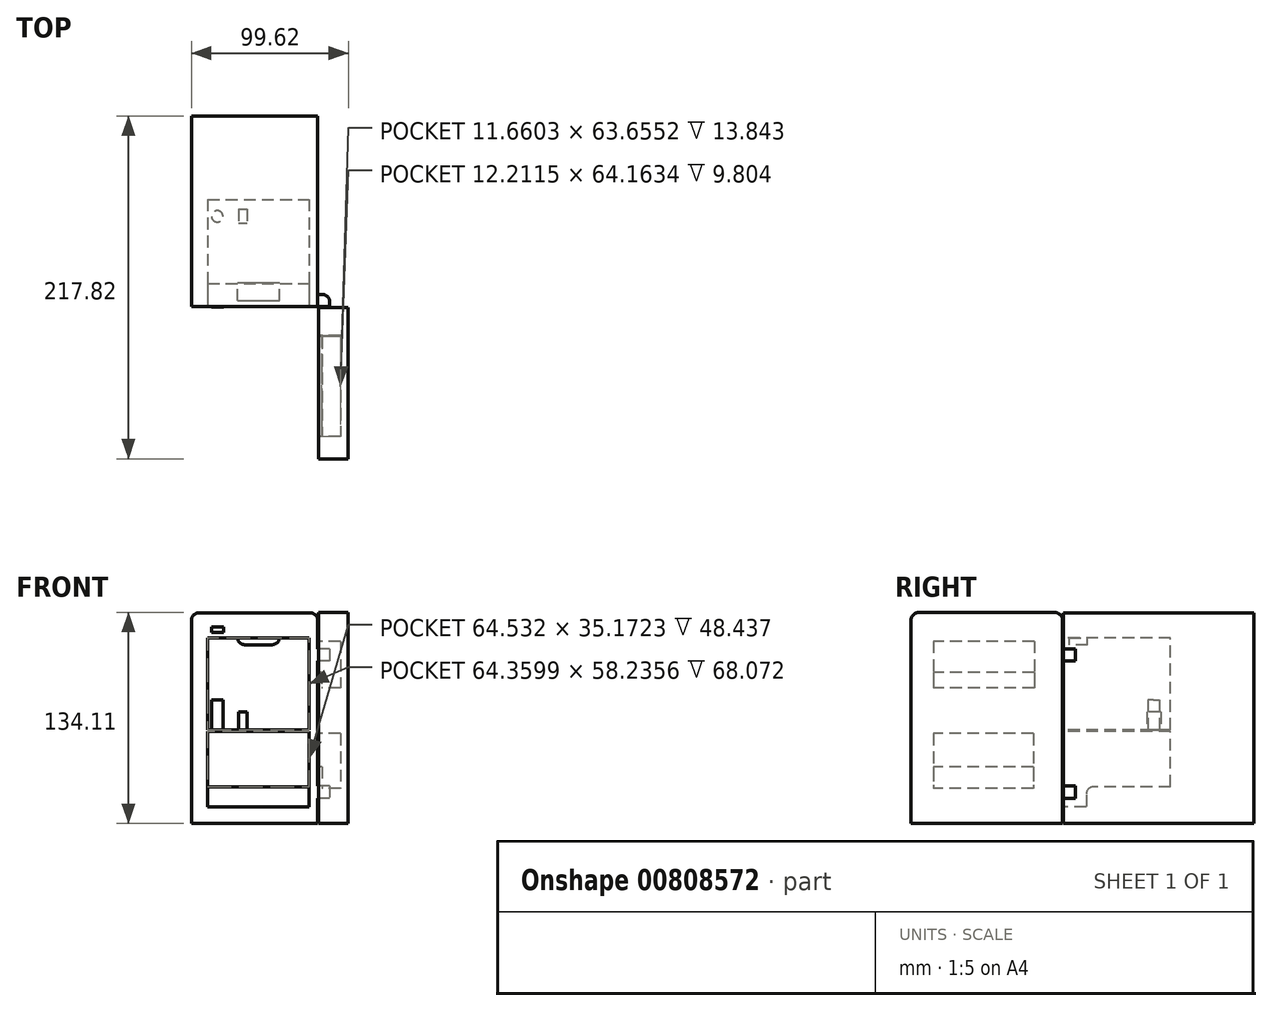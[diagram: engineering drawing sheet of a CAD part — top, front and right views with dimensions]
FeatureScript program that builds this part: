
annotation { "Feature Type Name" : "Feature", "Feature Type Description" : "" }
export const myFeature = defineFeature(function(context is Context, id is Id, definition is map)
    precondition{}
    {
        {
            var Q0;
            Q0=qCreatedBy(makeId("Top.planeOp"),FACE);
            var sketch = newSketch(context, id + "F0", { "sketchPlane" : qUnion([Q0])});
            skLineSegment(sketch, "E0.bottom", {"start": v(-38.44, 50.05) * mm, "end": v(41.76, 50.05) * mm});
            skLineSegment(sketch, "E0.top", {"start": v(-38.44, -71.07) * mm, "end": v(41.76, -71.07) * mm});
            skLineSegment(sketch, "E0.left", {"start": v(-38.44, 50.05) * mm, "end": v(-38.44, -71.07) * mm});
            skLineSegment(sketch, "E0.right", {"start": v(41.76, 50.05) * mm, "end": v(41.76, -71.07) * mm});
            skSolve(sketch);
        }
        {
            var Q0;
            Q0 = qSketchRegion(id + "F0", true);
            extrude(context, id + "F1", {"entities" : qUnion([Q0]), "depth" : 133.86 * mm, "offsetDistance" : 25.4 * mm});
        }
        {
            var Q0;
            Q0=qCreatedBy(makeId("Top.planeOp"),FACE);
            var sketch = newSketch(context, id + "F2", { "sketchPlane" : qUnion([Q0])});
            skLineSegment(sketch, "E1.bottom", {"start": v(42.32, -71.47) * mm, "end": v(61.18, -71.47) * mm});
            skLineSegment(sketch, "E1.top", {"start": v(42.32, -167.77) * mm, "end": v(61.18, -167.77) * mm});
            skLineSegment(sketch, "E1.left", {"start": v(42.32, -71.47) * mm, "end": v(42.32, -167.77) * mm});
            skLineSegment(sketch, "E1.right", {"start": v(61.18, -71.47) * mm, "end": v(61.18, -167.77) * mm});
            skSolve(sketch);
        }
        {
            var Q0;
            Q0=makeQuery(id+"F2.imprint","IMPRINT",FACE,{"disambiguationData":[TD([[makeQuery(id+"F2.imprint","IMPRINT",EDGE,{"derivedFrom":sQuery(id+"F2.wireOp",EDGE,"E1.bottom")}),-1.0]])]});
            extrude(context, id + "F3", {"entities" : qUnion([Q0]), "depth" : 134.11 * mm, "offsetDistance" : 25.4 * mm});
        }
        {
            var Q0;
            Q0=makeQuery(id+"F3.opExtrude","SWEPT_FACE",FACE,{"disambiguationData":[OSD([sQuery(id+"F2.wireOp",EDGE,"E1.left")])]});
            var sketch = newSketch(context, id + "F4", { "sketchPlane" : qUnion([Q0])});
            skLineSegment(sketch, "E2.bottom", {"start": v(89.5, 115.7) * mm, "end": v(153.66, 115.7) * mm});
            skLineSegment(sketch, "E2.top", {"start": v(89.5, 86.24) * mm, "end": v(153.66, 86.24) * mm});
            skLineSegment(sketch, "E2.left", {"start": v(89.5, 115.7) * mm, "end": v(89.5, 86.24) * mm});
            skLineSegment(sketch, "E2.right", {"start": v(153.66, 115.7) * mm, "end": v(153.66, 86.24) * mm});
            skLineSegment(sketch, "E3.bottom", {"start": v(90, 57.2) * mm, "end": v(153.66, 57.2) * mm});
            skLineSegment(sketch, "E3.top", {"start": v(90, 22.28) * mm, "end": v(153.66, 22.28) * mm});
            skLineSegment(sketch, "E3.left", {"start": v(90, 57.2) * mm, "end": v(90, 22.28) * mm});
            skLineSegment(sketch, "E3.right", {"start": v(153.66, 57.2) * mm, "end": v(153.66, 22.28) * mm});
            skSolve(sketch);
        }
        {
            var Q0;
            Q0=makeQuery(id+"F4.imprint","IMPRINT",FACE,{"disambiguationData":[TD([[makeQuery(id+"F4.imprint","IMPRINT",EDGE,{"derivedFrom":sQuery(id+"F4.wireOp",EDGE,"E2.bottom")}),-1.0]])]});
            var Q1;
            Q1=makeQuery(id+"F4.imprint","IMPRINT",FACE,{"disambiguationData":[TD([[makeQuery(id+"F4.imprint","IMPRINT",EDGE,{"derivedFrom":sQuery(id+"F4.wireOp",EDGE,"E3.bottom")}),-1.0]])]});
            extrude(context, id + "F5", {"entities" : qUnion([Q0, Q1]), "operationType" : NewBodyOperationType.REMOVE, "oppositeDirection" : true, "depth" : 13.97 * mm, "offsetDistance" : 25.4 * mm});
        }
        {
            var Q0;
            Q0=makeQuery(id+"F5.boolean.opBoolean","COPY",FACE,{"derivedFrom":makeQuery(id+"F5.opExtrude","SWEPT_FACE",FACE,{"disambiguationData":[OSD([sQuery(id+"F4.wireOp",EDGE,"E2.top")])]})});
            var sketch = newSketch(context, id + "F6", { "sketchPlane" : qUnion([Q0])});
            skLineSegment(sketch, "E4.bottom", {"start": v(44.08, -89.5) * mm, "end": v(42.32, -89.5) * mm});
            skLineSegment(sketch, "E4.top", {"start": v(44.08, -153.66) * mm, "end": v(42.32, -153.66) * mm});
            skLineSegment(sketch, "E4.left", {"start": v(44.08, -89.5) * mm, "end": v(44.08, -153.66) * mm});
            skLineSegment(sketch, "E4.right", {"start": v(42.32, -89.5) * mm, "end": v(42.32, -153.66) * mm});
            skSolve(sketch);
        }
        {
            var Q0;
            Q0=makeQuery(id+"F6.imprint","IMPRINT",FACE,{"disambiguationData":[TD([[makeQuery(id+"F6.imprint","IMPRINT",EDGE,{"derivedFrom":sQuery(id+"F6.wireOp",EDGE,"E4.bottom")}),1.0]])]});
            extrude(context, id + "F7", {"entities" : qUnion([Q0]), "operationType" : NewBodyOperationType.ADD, "depth" : 9.8 * mm, "offsetDistance" : 25.4 * mm});
        }
        {
            var Q0;
            Q0=makeQuery(id+"F5.boolean.opBoolean","COPY",FACE,{"derivedFrom":makeQuery(id+"F5.opExtrude","SWEPT_FACE",FACE,{"disambiguationData":[OSD([sQuery(id+"F4.wireOp",EDGE,"E3.top")])]})});
            var sketch = newSketch(context, id + "F8", { "sketchPlane" : qUnion([Q0])});
            skLineSegment(sketch, "E5.bottom", {"start": v(44.63, -90) * mm, "end": v(42.32, -90) * mm});
            skLineSegment(sketch, "E5.top", {"start": v(44.63, -153.66) * mm, "end": v(42.32, -153.66) * mm});
            skLineSegment(sketch, "E5.left", {"start": v(44.63, -90) * mm, "end": v(44.63, -153.66) * mm});
            skLineSegment(sketch, "E5.right", {"start": v(42.32, -90) * mm, "end": v(42.32, -153.66) * mm});
            skSolve(sketch);
        }
        {
            var Q0;
            Q0=makeQuery(id+"F8.imprint","IMPRINT",FACE,{"disambiguationData":[TD([[makeQuery(id+"F8.imprint","IMPRINT",EDGE,{"derivedFrom":sQuery(id+"F8.wireOp",EDGE,"E5.bottom")}),1.0]])]});
            extrude(context, id + "F9", {"entities" : qUnion([Q0]), "operationType" : NewBodyOperationType.ADD, "depth" : 13.84 * mm, "offsetDistance" : 25.4 * mm});
        }
        {
            var Q0;
            Q0=makeQuery(id+"F1.opExtrude","CAP_EDGE",EDGE,{"disambiguationData":[OSD([sQuery(id+"F0.wireOp",EDGE,"E0.left")])],"isStart":false});
            var Q1;
            Q1=makeQuery(id+"F1.opExtrude","CAP_EDGE",EDGE,{"disambiguationData":[OSD([sQuery(id+"F0.wireOp",EDGE,"E0.right")])],"isStart":false});
            var Q2;
            Q2=makeQuery(id+"F3.opExtrude","CAP_EDGE",EDGE,{"disambiguationData":[OSD([sQuery(id+"F2.wireOp",EDGE,"E1.top")])],"isStart":false});
            var Q3;
            Q3=makeQuery(id+"F3.opExtrude","CAP_EDGE",EDGE,{"disambiguationData":[OSD([sQuery(id+"F2.wireOp",EDGE,"E1.bottom")])],"isStart":false});
            fillet(context, id + "F10", {"entities" : qUnion([Q0, Q1, Q2, Q3]), "radius" : 5.08 * mm, "tangentPropagation" : true, "allowEdgeOverflow" : false});
        }
        {
            var Q0;
            Q0=makeQuery(id+"F1.opExtrude","SWEPT_FACE",FACE,{"disambiguationData":[OSD([sQuery(id+"F0.wireOp",EDGE,"E0.right")])]});
            var sketch = newSketch(context, id + "F11", { "sketchPlane" : qUnion([Q0])});
            skLineSegment(sketch, "E6.bottom", {"start": v(-71.07, 110.8) * mm, "end": v(-63.22, 110.8) * mm});
            skLineSegment(sketch, "E6.top", {"start": v(-71.07, 103.4) * mm, "end": v(-63.22, 103.4) * mm});
            skLineSegment(sketch, "E6.left", {"start": v(-71.07, 110.8) * mm, "end": v(-71.07, 103.4) * mm});
            skLineSegment(sketch, "E6.right", {"start": v(-63.22, 110.8) * mm, "end": v(-63.22, 103.4) * mm});
            skLineSegment(sketch, "E7.bottom", {"start": v(-71.07, 24.04) * mm, "end": v(-63.22, 24.04) * mm});
            skLineSegment(sketch, "E7.top", {"start": v(-71.07, 15.97) * mm, "end": v(-63.22, 15.97) * mm});
            skLineSegment(sketch, "E7.left", {"start": v(-71.07, 24.04) * mm, "end": v(-71.07, 15.97) * mm});
            skLineSegment(sketch, "E7.right", {"start": v(-63.22, 24.04) * mm, "end": v(-63.22, 15.97) * mm});
            skSolve(sketch);
        }
        {
            var Q0;
            Q0=makeQuery(id+"F11.imprint","IMPRINT",FACE,{"disambiguationData":[TD([[makeQuery(id+"F11.imprint","IMPRINT",EDGE,{"derivedFrom":sQuery(id+"F11.wireOp",EDGE,"E6.bottom")}),-1.0]])]});
            var Q1;
            Q1=makeQuery(id+"F11.imprint","IMPRINT",FACE,{"disambiguationData":[TD([[makeQuery(id+"F11.imprint","IMPRINT",EDGE,{"derivedFrom":sQuery(id+"F11.wireOp",EDGE,"E7.bottom")}),-1.0]])]});
            extrude(context, id + "F12", {"entities" : qUnion([Q0, Q1]), "operationType" : NewBodyOperationType.ADD, "depth" : 7.62 * mm, "offsetDistance" : 25.4 * mm});
        }
        {
            var Q0;
            Q0=makeQuery(id+"F12.opExtrude","CAP_EDGE",EDGE,{"disambiguationData":[OSD([sQuery(id+"F11.wireOp",EDGE,"E6.right")])],"isStart":false});
            var Q1;
            Q1=makeQuery(id+"F12.opExtrude","CAP_EDGE",EDGE,{"disambiguationData":[OSD([sQuery(id+"F11.wireOp",EDGE,"E7.right")])],"isStart":false});
            fillet(context, id + "F13", {"entities" : qUnion([Q0, Q1]), "radius" : 5.08 * mm, "tangentPropagation" : true, "allowEdgeOverflow" : false});
        }
        {
            var Q0;
            Q0=makeQuery(id+"F12.boolean.opBoolean","MERGE",FACE,{"derivedFrom":[makeQuery(id+"F1.opExtrude","SWEPT_FACE",FACE,{"disambiguationData":[OSD([sQuery(id+"F0.wireOp",EDGE,"E0.top")])]}),makeQuery(id+"F12.opExtrude","SWEPT_FACE",FACE,{"disambiguationData":[OSD([sQuery(id+"F11.wireOp",EDGE,"E6.left")])]}),makeQuery(id+"F12.opExtrude","SWEPT_FACE",FACE,{"disambiguationData":[OSD([sQuery(id+"F11.wireOp",EDGE,"E7.left")])]})]});
            var sketch = newSketch(context, id + "F14", { "sketchPlane" : qUnion([Q0])});
            skLineSegment(sketch, "E8.bottom", {"start": v(-28.17, 10.71) * mm, "end": v(36.36, 10.71) * mm});
            skLineSegment(sketch, "E8.top", {"start": v(-28.17, 58.58) * mm, "end": v(36.36, 58.58) * mm});
            skLineSegment(sketch, "E8.left", {"start": v(-28.17, 10.71) * mm, "end": v(-28.17, 58.58) * mm});
            skLineSegment(sketch, "E8.right", {"start": v(36.36, 10.71) * mm, "end": v(36.36, 58.58) * mm});
            skLineSegment(sketch, "E9.bottom", {"start": v(-28.17, 66.66) * mm, "end": v(36.2, 66.66) * mm});
            skLineSegment(sketch, "E9.top", {"start": v(-28.17, 117.78) * mm, "end": v(36.2, 117.78) * mm});
            skLineSegment(sketch, "E9.left", {"start": v(-28.17, 66.66) * mm, "end": v(-28.17, 117.78) * mm});
            skLineSegment(sketch, "E9.right", {"start": v(36.2, 66.66) * mm, "end": v(36.2, 117.78) * mm});
            skSolve(sketch);
        }
        {
            var Q0;
            Q0=makeQuery(id+"F14.imprint","IMPRINT",FACE,{"disambiguationData":[TD([[makeQuery(id+"F14.imprint","IMPRINT",EDGE,{"derivedFrom":sQuery(id+"F14.wireOp",EDGE,"E9.bottom")}),1.0]])]});
            var Q1;
            Q1=makeQuery(id+"F14.imprint","IMPRINT",FACE,{"disambiguationData":[TD([[makeQuery(id+"F14.imprint","IMPRINT",EDGE,{"derivedFrom":sQuery(id+"F14.wireOp",EDGE,"E8.bottom")}),1.0]])]});
            extrude(context, id + "F15", {"entities" : qUnion([Q0, Q1]), "operationType" : NewBodyOperationType.REMOVE, "oppositeDirection" : true, "depth" : 68.07 * mm, "offsetDistance" : 25.4 * mm});
        }
        {
            var Q0;
            Q0=makeQuery(id+"F15.boolean.opBoolean","COPY",FACE,{"derivedFrom":makeQuery(id+"F15.opExtrude","SWEPT_FACE",FACE,{"disambiguationData":[OSD([sQuery(id+"F14.wireOp",EDGE,"E9.bottom")])]})});
            extrude(context, id + "F16", {"entities" : qUnion([Q0]), "operationType" : NewBodyOperationType.REMOVE, "oppositeDirection" : true, "depth" : 7.11 * mm, "offsetDistance" : 25.4 * mm});
        }
        {
            var Q0;
            Q0=makeQuery(id+"F15.boolean.opBoolean","COPY",FACE,{"derivedFrom":makeQuery(id+"F15.opExtrude","SWEPT_FACE",FACE,{"disambiguationData":[OSD([sQuery(id+"F14.wireOp",EDGE,"E8.bottom")])]})});
            var sketch = newSketch(context, id + "F17", { "sketchPlane" : qUnion([Q0])});
            skLineSegment(sketch, "E10.bottom", {"start": v(-28.17, -56.51) * mm, "end": v(0, -56.51) * mm});
            skLineSegment(sketch, "E10.top", {"start": v(-28.17, -3) * mm, "end": v(0, -3) * mm});
            skLineSegment(sketch, "E10.left", {"start": v(-28.17, -56.51) * mm, "end": v(-28.17, -3) * mm});
            skLineSegment(sketch, "E10.right", {"start": v(0, -56.51) * mm, "end": v(0, -3) * mm});
            skLineSegment(sketch, "E11.bottom", {"start": v(0, -56.51) * mm, "end": v(36.36, -56.51) * mm});
            skLineSegment(sketch, "E11.top", {"start": v(0, -3) * mm, "end": v(36.36, -3) * mm});
            skLineSegment(sketch, "E11.right", {"start": v(36.36, -56.51) * mm, "end": v(36.36, -3) * mm});
            skSolve(sketch);
        }
        {
            var Q0;
            Q0=makeQuery(id+"F17.imprint","IMPRINT",FACE,{"disambiguationData":[TD([[makeQuery(id+"F17.imprint","IMPRINT",EDGE,{"derivedFrom":sQuery(id+"F17.wireOp",EDGE,"E10.bottom")}),1.0]])]});
            var Q1;
            Q1=makeQuery(id+"F17.imprint","IMPRINT",FACE,{"disambiguationData":[TD([[makeQuery(id+"F17.imprint","IMPRINT",EDGE,{"derivedFrom":sQuery(id+"F17.wireOp",EDGE,"E11.bottom")}),1.0]])]});
            extrude(context, id + "F18", {"entities" : qUnion([Q0, Q1]), "operationType" : NewBodyOperationType.ADD, "depth" : 12.7 * mm, "offsetDistance" : 25.4 * mm});
        }
        {
            var Q0;
            Q0=makeQuery(id+"F18.opExtrude","CAP_EDGE",EDGE,{"disambiguationData":[OSD([sQuery(id+"F17.wireOp",EDGE,"E10.bottom"),sQuery(id+"F17.wireOp",EDGE,"E11.bottom")])],"isStart":false});
            fillet(context, id + "F19", {"entities" : qUnion([Q0]), "radius" : 5.08 * mm, "tangentPropagation" : true, "allowEdgeOverflow" : false});
        }
        {
            var Q0;
            Q0=makeQuery(id+"F12.boolean.opBoolean","MERGE",FACE,{"derivedFrom":[makeQuery(id+"F1.opExtrude","SWEPT_FACE",FACE,{"disambiguationData":[OSD([sQuery(id+"F0.wireOp",EDGE,"E0.top")])]}),makeQuery(id+"F12.opExtrude","SWEPT_FACE",FACE,{"disambiguationData":[OSD([sQuery(id+"F11.wireOp",EDGE,"E6.left")])]}),makeQuery(id+"F12.opExtrude","SWEPT_FACE",FACE,{"disambiguationData":[OSD([sQuery(id+"F11.wireOp",EDGE,"E7.left")])]})]});
            var sketch = newSketch(context, id + "F20", { "sketchPlane" : qUnion([Q0])});
            skLineSegment(sketch, "E12.bottom", {"start": v(-25.78, 121.5) * mm, "end": v(-18, 121.5) * mm});
            skLineSegment(sketch, "E12.top", {"start": v(-25.78, 125) * mm, "end": v(-18, 125) * mm});
            skLineSegment(sketch, "E12.left", {"start": v(-25.78, 121.5) * mm, "end": v(-25.78, 125) * mm});
            skLineSegment(sketch, "E12.right", {"start": v(-18, 121.5) * mm, "end": v(-18, 125) * mm});
            skSolve(sketch);
        }
        {
            var Q0;
            Q0=makeQuery(id+"F20.imprint","IMPRINT",FACE,{"disambiguationData":[TD([[makeQuery(id+"F20.imprint","IMPRINT",EDGE,{"derivedFrom":sQuery(id+"F20.wireOp",EDGE,"E12.bottom")}),1.0]])]});
            extrude(context, id + "F21", {"entities" : qUnion([Q0]), "operationType" : NewBodyOperationType.ADD, "depth" : 0.23 * mm, "offsetDistance" : 25.4 * mm});
        }
        {
            var Q0;
            Q0=makeQuery(id+"F15.boolean.opBoolean","COPY",FACE,{"derivedFrom":makeQuery(id+"F15.opExtrude","SWEPT_FACE",FACE,{"disambiguationData":[OSD([sQuery(id+"F14.wireOp",EDGE,"E9.top")])]})});
            var sketch = newSketch(context, id + "F22", { "sketchPlane" : qUnion([Q0])});
            skLineSegment(sketch, "E13.bottom", {"start": v(-9.29, 67.33) * mm, "end": v(17.64, 67.33) * mm});
            skLineSegment(sketch, "E13.top", {"start": v(-9.29, 55.68) * mm, "end": v(17.64, 55.68) * mm});
            skLineSegment(sketch, "E13.left", {"start": v(-9.29, 67.33) * mm, "end": v(-9.29, 55.68) * mm});
            skLineSegment(sketch, "E13.right", {"start": v(17.64, 67.33) * mm, "end": v(17.64, 55.68) * mm});
            skSolve(sketch);
        }
        {
            var Q0;
            Q0=makeQuery(id+"F22.imprint","IMPRINT",FACE,{"disambiguationData":[TD([[makeQuery(id+"F22.imprint","IMPRINT",EDGE,{"derivedFrom":sQuery(id+"F22.wireOp",EDGE,"E13.bottom")}),-1.0]])]});
            extrude(context, id + "F23", {"entities" : qUnion([Q0]), "operationType" : NewBodyOperationType.ADD, "depth" : 4.24 * mm, "offsetDistance" : 25.4 * mm});
        }
        {
            var Q0;
            Q0=makeQuery(id+"F23.opExtrude","CAP_EDGE",EDGE,{"disambiguationData":[OSD([sQuery(id+"F22.wireOp",EDGE,"E13.left")])],"isStart":false});
            var Q1;
            Q1=makeQuery(id+"F23.opExtrude","CAP_EDGE",EDGE,{"disambiguationData":[OSD([sQuery(id+"F22.wireOp",EDGE,"E13.right")])],"isStart":false});
            fillet(context, id + "F24", {"entities" : qUnion([Q0, Q1]), "radius" : 5.08 * mm, "tangentPropagation" : true, "allowEdgeOverflow" : false});
        }
        {
            var Q0;
            Q0=makeQuery(id+"F16.boolean.opBoolean","COPY",FACE,{"derivedFrom":makeQuery(id+"F16.opExtrude","CAP_FACE",FACE,{"disambiguationData":[OSD([sQuery(id+"F14.wireOp",EDGE,"E9.bottom")])],"isStart":false})});
            var sketch = newSketch(context, id + "F25", { "sketchPlane" : qUnion([Q0])});
            skCircle(sketch, "E14", {"center": v(-22.06, -13.7) * mm, "radius": 3.62 * mm});
            skSolve(sketch);
        }
        {
            var Q0;
            Q0=makeQuery(id+"F25.imprint","IMPRINT",FACE,{"disambiguationData":[TD([[makeQuery(id+"F25.imprint","IMPRINT",EDGE,{"derivedFrom":sQuery(id+"F25.wireOp",EDGE,"E14")}),1.0]])]});
            extrude(context, id + "F26", {"entities" : qUnion([Q0]), "operationType" : NewBodyOperationType.ADD, "depth" : 18.97 * mm, "offsetDistance" : 25.4 * mm});
        }
        {
            var Q0;
            Q0=makeQuery(id+"F16.boolean.opBoolean","COPY",FACE,{"derivedFrom":makeQuery(id+"F16.opExtrude","CAP_FACE",FACE,{"disambiguationData":[OSD([sQuery(id+"F14.wireOp",EDGE,"E9.bottom")])],"isStart":false})});
            var sketch = newSketch(context, id + "F27", { "sketchPlane" : qUnion([Q0])});
            skLineSegment(sketch, "E15.bottom", {"start": v(-8.46, -9.2) * mm, "end": v(-3.2, -9.2) * mm});
            skLineSegment(sketch, "E15.top", {"start": v(-8.46, -17.99) * mm, "end": v(-3.2, -17.99) * mm});
            skLineSegment(sketch, "E15.left", {"start": v(-8.46, -9.2) * mm, "end": v(-8.46, -17.99) * mm});
            skLineSegment(sketch, "E15.right", {"start": v(-3.2, -9.2) * mm, "end": v(-3.2, -17.99) * mm});
            skSolve(sketch);
        }
        {
            var Q0;
            Q0=makeQuery(id+"F27.imprint","IMPRINT",FACE,{"disambiguationData":[TD([[makeQuery(id+"F27.imprint","IMPRINT",EDGE,{"derivedFrom":sQuery(id+"F27.wireOp",EDGE,"E15.bottom")}),-1.0]])]});
            extrude(context, id + "F28", {"entities" : qUnion([Q0]), "operationType" : NewBodyOperationType.ADD, "depth" : 11.23 * mm, "offsetDistance" : 25.4 * mm});
        }
    });
